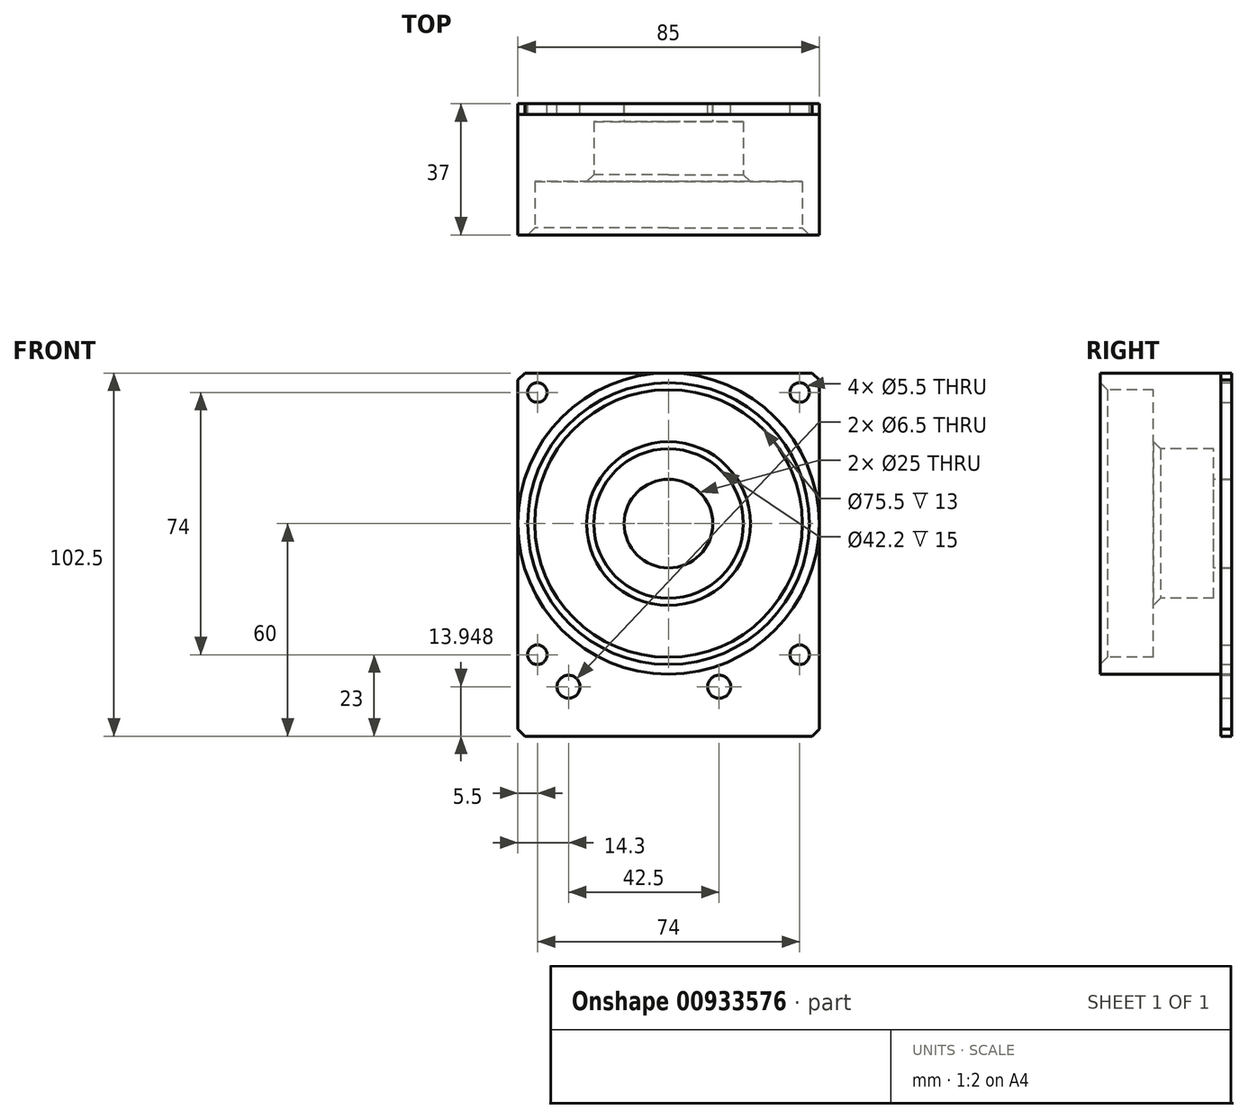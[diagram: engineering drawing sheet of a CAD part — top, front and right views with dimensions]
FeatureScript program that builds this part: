
annotation { "Feature Type Name" : "Feature", "Feature Type Description" : "" }
export const myFeature = defineFeature(function(context is Context, id is Id, definition is map)
    precondition{}
    {
        {
            var Q0;
            Q0=qCreatedBy(makeId("Right.planeOp"),FACE);
            var sketch = newSketch(context, id + "F0", { "sketchPlane" : qUnion([Q0])});
            skLineSegment(sketch, "E0", {"start": v(0, 42.5) * mm, "end": v(-37, 42.5) * mm});
            skLineSegment(sketch, "E1", {"start": v(-37, 42.5) * mm, "end": v(-37, 37.75) * mm});
            skLineSegment(sketch, "E2", {"start": v(-37, 37.75) * mm, "end": v(-22, 37.75) * mm});
            skLineSegment(sketch, "E3", {"start": v(-22, 37.75) * mm, "end": v(-22, 21.1) * mm});
            skLineSegment(sketch, "E4", {"start": v(-22, 21.1) * mm, "end": v(-5, 21.1) * mm});
            skLineSegment(sketch, "E5", {"start": v(-13.02, 0) * mm, "end": v(4.1, 0) * mm, "construction": true});
            skLineSegment(sketch, "E6", {"start": v(-5, 21.1) * mm, "end": v(-5, 12.5) * mm});
            skLineSegment(sketch, "E7", {"start": v(-5, 12.5) * mm, "end": v(0, 12.5) * mm});
            skLineSegment(sketch, "E8", {"start": v(0, 12.5) * mm, "end": v(0, 42.5) * mm});
            skSolve(sketch);
        }
        {
            var Q0;
            Q0=qSketchRegion(id+"F0",true);
            var Q1;
            Q1=sQuery(id+"F0.wireOp",EDGE,"E5");
            revolve(context, id + "F1", {"surfaceOperationType" : NewSurfaceOperationType.NEW, "entities" : qUnion([Q0]), "axis" : qUnion([Q1]), "revolveType" : RevolveType.FULL});
        }
        {
            var Q0;
            Q0=qCreatedBy(makeId("Front.planeOp"),FACE);
            var sketch = newSketch(context, id + "F2", { "sketchPlane" : qUnion([Q0])});
            skLineSegment(sketch, "E9.bottom", {"start": v(42.5, 42.5) * mm, "end": v(-42.5, 42.5) * mm});
            skLineSegment(sketch, "E9.left", {"start": v(42.5, 42.5) * mm, "end": v(42.5, -42.5) * mm});
            skLineSegment(sketch, "E9.right", {"start": v(-42.5, 42.5) * mm, "end": v(-42.5, -42.5) * mm});
            skPoint(sketch, "E9.middle", {"position": v(0, 0) * mm});
            skCircle(sketch, "E10", {"center": v(-37, 37) * mm, "radius": 2.75 * mm});
            skCircle(sketch, "E11.MirrorC", {"center": v(37, 37) * mm, "radius": 2.75 * mm});
            skCircle(sketch, "E12.MirrorC", {"center": v(-37, -37) * mm, "radius": 2.75 * mm});
            skCircle(sketch, "E13.MirrorC", {"center": v(37, -37) * mm, "radius": 2.75 * mm});
            skCircle(sketch, "E14", {"center": v(0, 0) * mm, "radius": 12.5 * mm});
            skLineSegment(sketch, "E15.top", {"start": v(42.5, -60) * mm, "end": v(-42.5, -60) * mm});
            skLineSegment(sketch, "E15.left", {"start": v(42.5, 0) * mm, "end": v(42.5, -60) * mm});
            skLineSegment(sketch, "E15.right", {"start": v(-42.5, 0) * mm, "end": v(-42.5, -60) * mm});
            skCircle(sketch, "E16", {"center": v(14.3, -46.05) * mm, "radius": 3.25 * mm});
            skCircle(sketch, "E17", {"center": v(-28.2, -46.05) * mm, "radius": 3.25 * mm});
            skSolve(sketch);
        }
        {
            var Q0;
            Q0=qSketchRegion(id+"F2",true);
            extrude(context, id + "F3", {"entities" : qUnion([Q0]), "depth" : 3 * mm, "offsetDistance" : 25 * mm});
        }
        {
            var Q0;
            Q0=makeQuery(id+"F3.opExtrude","SWEPT_EDGE",EDGE,{"disambiguationData":[OSD([sQuery(id+"F2.wireOp",EDGE,"E9.bottom"),sQuery(id+"F2.wireOp",EDGE,"E9.left")])]});
            var Q1;
            Q1=makeQuery(id+"F3.opExtrude","SWEPT_EDGE",EDGE,{"disambiguationData":[OSD([sQuery(id+"F2.wireOp",EDGE,"E9.bottom"),sQuery(id+"F2.wireOp",EDGE,"E9.right")])]});
            var Q2;
            Q2=makeQuery(id+"F3.opExtrude","SWEPT_EDGE",EDGE,{"disambiguationData":[OSD([sQuery(id+"F2.wireOp",EDGE,"E15.top"),sQuery(id+"F2.wireOp",EDGE,"E15.left")])]});
            var Q3;
            Q3=makeQuery(id+"F3.opExtrude","SWEPT_EDGE",EDGE,{"disambiguationData":[OSD([sQuery(id+"F2.wireOp",EDGE,"E15.top"),sQuery(id+"F2.wireOp",EDGE,"E15.right")])]});
            var Q4;
            Q4=makeQuery(id+"F1.opRevolve","SWEPT_EDGE",EDGE,{"disambiguationData":[OSD([sQuery(id+"F0.wireOp",EDGE,"E3"),sQuery(id+"F0.wireOp",EDGE,"E4")])]});
            var Q5;
            Q5=makeQuery(id+"F1.opRevolve","SWEPT_EDGE",EDGE,{"disambiguationData":[OSD([sQuery(id+"F0.wireOp",EDGE,"E1"),sQuery(id+"F0.wireOp",EDGE,"E2")])]});
            chamfer(context, id + "F4", {"entities" : qUnion([Q0, Q1, Q2, Q3, Q4, Q5]), "width" : 2 * mm, "tangentPropagation" : true});
        }
    });
